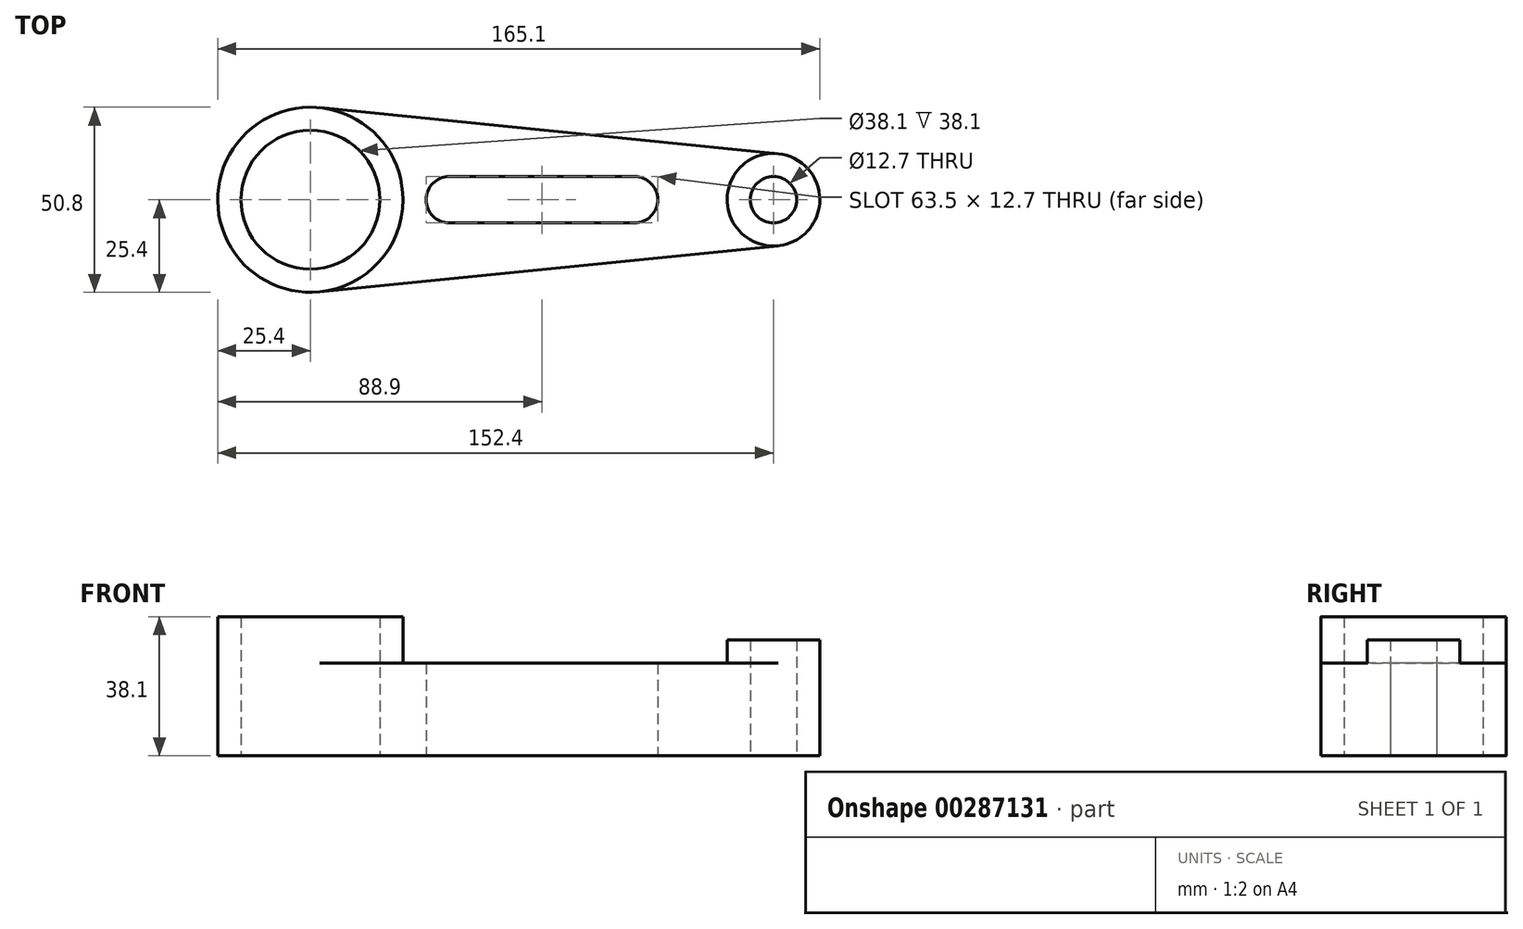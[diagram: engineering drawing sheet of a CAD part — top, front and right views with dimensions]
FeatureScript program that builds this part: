
annotation { "Feature Type Name" : "Feature", "Feature Type Description" : "" }
export const myFeature = defineFeature(function(context is Context, id is Id, definition is map)
    precondition{}
    {
        {
            var Q0;
            Q0=qCreatedBy(makeId("Top.planeOp"),FACE);
            var sketch = newSketch(context, id + "F0", { "sketchPlane" : qUnion([Q0])});
            skArc(sketch, "E0", {"start": v(0, 6.35) * mm, "mid": v(-6.35, 0) * mm, "end": v(0, -6.35) * mm});
            skArc(sketch, "E1", {"start": v(50.8, -6.35) * mm, "mid": v(57.15, 0) * mm, "end": v(50.8, 6.35) * mm});
            skLineSegment(sketch, "E2", {"start": v(0, 6.35) * mm, "end": v(50.8, 6.35) * mm});
            skLineSegment(sketch, "E3", {"start": v(0, -6.35) * mm, "end": v(50.8, -6.35) * mm});
            skCircle(sketch, "E4", {"center": v(-38.1, 0) * mm, "radius": 19.05 * mm});
            skCircle(sketch, "E5", {"center": v(-38.1, 0) * mm, "radius": 25.4 * mm});
            skCircle(sketch, "E6", {"center": v(88.9, 0) * mm, "radius": 6.35 * mm});
            skCircle(sketch, "E7", {"center": v(88.9, 0) * mm, "radius": 12.7 * mm});
            skLineSegment(sketch, "E8", {"start": v(-35.56, 25.27) * mm, "end": v(90.17, 12.64) * mm});
            skLineSegment(sketch, "E9", {"start": v(90.17, -12.64) * mm, "end": v(-35.56, -25.27) * mm});
            skSolve(sketch);
        }
        {
            var Q0;
            Q0=makeQuery(id+"F0.imprint","IMPRINT",FACE,{"disambiguationData":[TD([[makeQuery(id+"F0.imprint","IMPRINT",EDGE,{"derivedFrom":sQuery(id+"F0.wireOp",EDGE,"E0")}),-1.0]])]});
            extrude(context, id + "F1", {"entities" : qUnion([Q0]), "depth" : 25.4 * mm});
        }
        {
            var Q0;
            Q0=makeQuery(id+"F0.imprint","IMPRINT",FACE,{"disambiguationData":[TD([[makeQuery(id+"F0.imprint","IMPRINT",EDGE,{"derivedFrom":sQuery(id+"F0.wireOp",EDGE,"E4")}),-1.0]])]});
            extrude(context, id + "F2", {"entities" : qUnion([Q0]), "operationType" : NewBodyOperationType.ADD, "depth" : 38.1 * mm});
        }
        {
            var Q0;
            Q0=makeQuery(id+"F0.imprint","IMPRINT",FACE,{"disambiguationData":[TD([[makeQuery(id+"F0.imprint","IMPRINT",EDGE,{"derivedFrom":sQuery(id+"F0.wireOp",EDGE,"E6")}),-1.0]])]});
            extrude(context, id + "F3", {"entities" : qUnion([Q0]), "operationType" : NewBodyOperationType.ADD, "depth" : 31.75 * mm});
        }
    });
